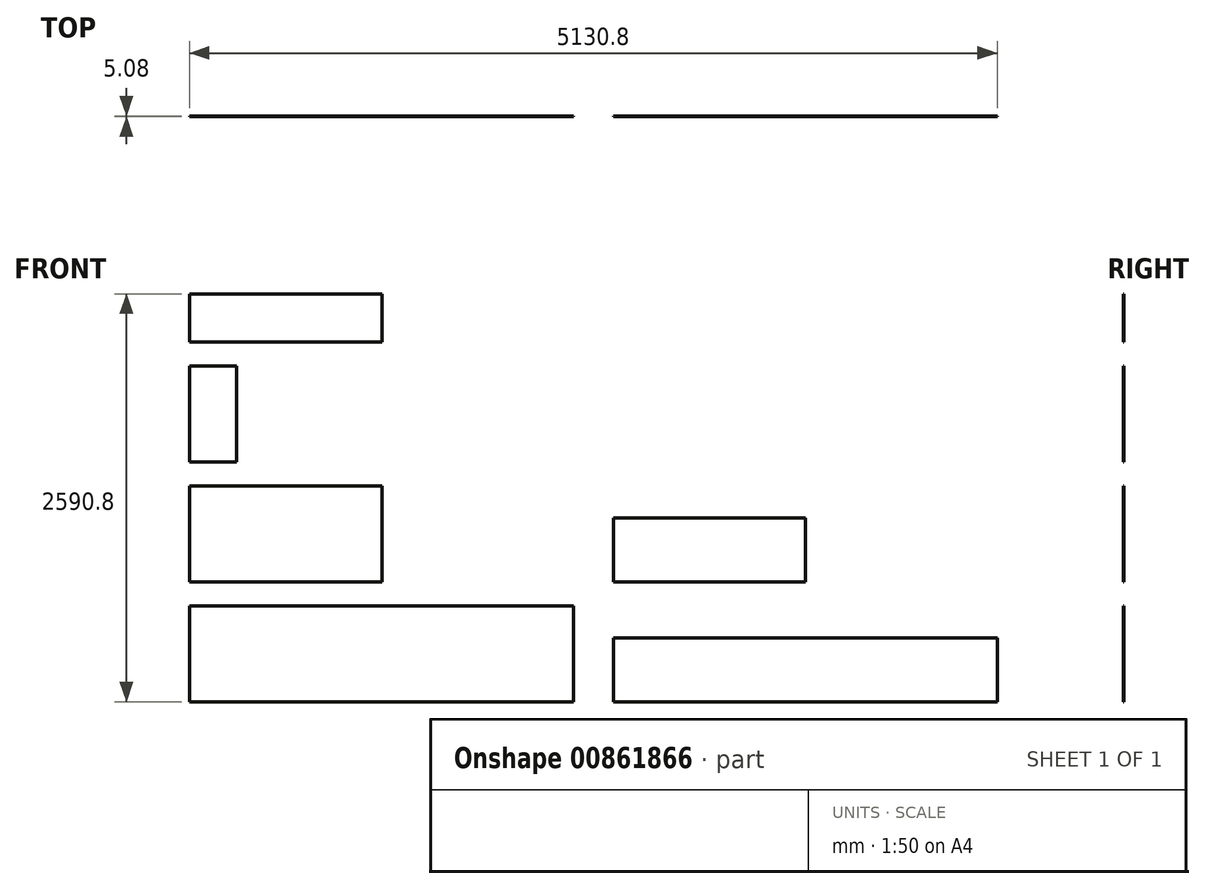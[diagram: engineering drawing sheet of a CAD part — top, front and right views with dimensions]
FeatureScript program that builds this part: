
annotation { "Feature Type Name" : "Feature", "Feature Type Description" : "" }
export const myFeature = defineFeature(function(context is Context, id is Id, definition is map)
    precondition{}
    {
        {
            var Q0;
            Q0=qCreatedBy(makeId("Front.planeOp"),FACE);
            var sketch = newSketch(context, id + "F0", { "sketchPlane" : qUnion([Q0])});
            skLineSegment(sketch, "E0.bottom", {"start": v(1219.2, -304.8) * mm, "end": v(-1219.2, -304.8) * mm});
            skLineSegment(sketch, "E0.top", {"start": v(1219.2, 304.8) * mm, "end": v(-1219.2, 304.8) * mm});
            skLineSegment(sketch, "E0.left", {"start": v(1219.2, -304.8) * mm, "end": v(1219.2, 304.8) * mm});
            skLineSegment(sketch, "E0.right", {"start": v(-1219.2, -304.8) * mm, "end": v(-1219.2, 304.8) * mm});
            skPoint(sketch, "E0.middle", {"position": v(0, 0) * mm});
            skSolve(sketch);
        }
        {
            var Q0;
            Q0=makeQuery(id+"F0.imprint","IMPRINT",FACE,{"disambiguationData":[TD([[makeQuery(id+"F0.imprint","IMPRINT",EDGE,{"derivedFrom":sQuery(id+"F0.wireOp",EDGE,"E0.bottom")}),-1.0]])]});
            extrude(context, id + "F1", {"entities" : qUnion([Q0]), "depth" : 5.08 * mm});
        }
        {
            var Q0;
            Q0=makeQuery(id+"F1.opExtrude","SWEPT_BODY",BODY,{"disambiguationData":[OSD([sQuery(id+"F0.wireOp",EDGE,"E0.bottom"),sQuery(id+"F0.wireOp",EDGE,"E0.top"),sQuery(id+"F0.wireOp",EDGE,"E0.left"),sQuery(id+"F0.wireOp",EDGE,"E0.right")])]});
            transform(context, id + "F2", {"entities" : qUnion([Q0]), "transformType" : TransformType.TRANSLATION_3D, "dx" : 0 * mm, "dy" : 0 * mm, "dz" : 914.4 * mm, "makeCopy" : true});
        }
        {
            var Q0;
            Q0=makeQuery(id+"F2.opPattern","COPY",FACE,{"derivedFrom":makeQuery(id+"F1.opExtrude","SWEPT_FACE",FACE,{"disambiguationData":[OSD([sQuery(id+"F0.wireOp",EDGE,"E0.left")])]}),"instanceName":"1"});
            extrude(context, id + "F3", {"entities" : qUnion([Q0]), "operationType" : NewBodyOperationType.ADD, "depth" : 609.6 * mm});
        }
        {
            var Q0;
            Q0=makeQuery(id+"F2.opPattern","COPY",BODY,{"derivedFrom":makeQuery(id+"F1.opExtrude","SWEPT_BODY",BODY,{"disambiguationData":[OSD([sQuery(id+"F0.wireOp",EDGE,"E0.bottom"),sQuery(id+"F0.wireOp",EDGE,"E0.top"),sQuery(id+"F0.wireOp",EDGE,"E0.left"),sQuery(id+"F0.wireOp",EDGE,"E0.right")])]}),"instanceName":"1"});
            deleteBodies(context, id + "F4", {"entities" : qUnion([Q0])});
        }
        {
            var Q0;
            Q0=makeQuery(id+"F1.opExtrude","SWEPT_BODY",BODY,{"disambiguationData":[OSD([sQuery(id+"F0.wireOp",EDGE,"E0.bottom"),sQuery(id+"F0.wireOp",EDGE,"E0.top"),sQuery(id+"F0.wireOp",EDGE,"E0.left"),sQuery(id+"F0.wireOp",EDGE,"E0.right")])]});
            transform(context, id + "F5", {"entities" : qUnion([Q0]), "transformType" : TransformType.TRANSLATION_3D, "dx" : 0 * mm, "dy" : 0 * mm, "dz" : 762 * mm, "makeCopy" : true});
        }
        {
            var Q0;
            Q0=makeQuery(id+"F5.opPattern","COPY",FACE,{"derivedFrom":makeQuery(id+"F1.opExtrude","SWEPT_FACE",FACE,{"disambiguationData":[OSD([sQuery(id+"F0.wireOp",EDGE,"E0.left")])]}),"instanceName":"1"});
            extrude(context, id + "F6", {"entities" : qUnion([Q0]), "operationType" : NewBodyOperationType.REMOVE, "oppositeDirection" : true, "depth" : 1219.2 * mm});
        }
        {
            var Q0;
            Q0=makeQuery(id+"F5.opPattern","COPY",BODY,{"derivedFrom":makeQuery(id+"F1.opExtrude","SWEPT_BODY",BODY,{"disambiguationData":[OSD([sQuery(id+"F0.wireOp",EDGE,"E0.bottom"),sQuery(id+"F0.wireOp",EDGE,"E0.top"),sQuery(id+"F0.wireOp",EDGE,"E0.left"),sQuery(id+"F0.wireOp",EDGE,"E0.right")])]}),"instanceName":"1"});
            transform(context, id + "F7", {"entities" : qUnion([Q0]), "transformType" : TransformType.TRANSLATION_3D, "dx" : 0 * mm, "dy" : 0 * mm, "dz" : 762 * mm, "makeCopy" : true});
        }
        {
            var Q0;
            Q0=makeQuery(id+"F7.opPattern","COPY",FACE,{"derivedFrom":makeQuery(id+"F6.boolean.opBoolean","COPY",FACE,{"derivedFrom":makeQuery(id+"F6.opExtrude","CAP_FACE",FACE,{"disambiguationData":[OSD([sQuery(id+"F0.wireOp",EDGE,"E0.left")])],"isStart":false})}),"instanceName":"1"});
            extrude(context, id + "F8", {"entities" : qUnion([Q0]), "operationType" : NewBodyOperationType.REMOVE, "oppositeDirection" : true, "depth" : 304.8 * mm});
        }
        {
            var Q0;
            Q0=makeQuery(id+"F8.boolean.opBoolean","COPY",FACE,{"derivedFrom":makeQuery(id+"F8.opExtrude","CAP_FACE",FACE,{"disambiguationData":[OSD([sQuery(id+"F0.wireOp",EDGE,"E0.left")])],"isStart":false})});
            extrude(context, id + "F9", {"entities" : qUnion([Q0]), "operationType" : NewBodyOperationType.REMOVE, "oppositeDirection" : true, "depth" : 609.6 * mm});
        }
        {
            var Q0;
            Q0=makeQuery(id+"F9.boolean.opBoolean","COPY",FACE,{"derivedFrom":makeQuery(id+"F9.opExtrude","CAP_FACE",FACE,{"disambiguationData":[OSD([sQuery(id+"F0.wireOp",EDGE,"E0.left")])],"isStart":false})});
            extrude(context, id + "F10", {"entities" : qUnion([Q0]), "operationType" : NewBodyOperationType.ADD, "depth" : 6.35 * mm});
        }
        {
            var Q0;
            Q0=makeQuery(id+"F10.opExtrude","CAP_FACE",FACE,{"disambiguationData":[OSD([sQuery(id+"F0.wireOp",EDGE,"E0.left")])],"isStart":false});
            extrude(context, id + "F11", {"entities" : qUnion([Q0]), "operationType" : NewBodyOperationType.REMOVE, "oppositeDirection" : true, "depth" : 11.43 * mm});
        }
        {
            var Q0;
            Q0=makeQuery(id+"F6.boolean.opBoolean","COPY",FACE,{"derivedFrom":makeQuery(id+"F6.opExtrude","CAP_FACE",FACE,{"disambiguationData":[OSD([sQuery(id+"F0.wireOp",EDGE,"E0.left")])],"isStart":false})});
            extrude(context, id + "F12", {"entities" : qUnion([Q0]), "operationType" : NewBodyOperationType.ADD, "depth" : 5.08 * mm});
        }
        {
            var Q0;
            Q0=makeQuery(id+"F5.opPattern","COPY",BODY,{"derivedFrom":makeQuery(id+"F1.opExtrude","SWEPT_BODY",BODY,{"disambiguationData":[OSD([sQuery(id+"F0.wireOp",EDGE,"E0.bottom"),sQuery(id+"F0.wireOp",EDGE,"E0.top"),sQuery(id+"F0.wireOp",EDGE,"E0.left"),sQuery(id+"F0.wireOp",EDGE,"E0.right")])]}),"instanceName":"1"});
            transform(context, id + "F13", {"entities" : qUnion([Q0]), "transformType" : TransformType.TRANSLATION_3D, "dx" : 0 * mm, "dy" : 0 * mm, "dz" : 1524 * mm, "makeCopy" : true});
        }
        {
            var Q0;
            {var subQ0=sQuery(id+"F0.wireOp",EDGE,"E0.top");Q0=makeQuery(id+"F13.opPattern","COPY",FACE,{"derivedFrom":makeQuery(id+"F12.boolean.opBoolean","MERGE",FACE,{"derivedFrom":[makeQuery(id+"F5.opPattern","COPY",FACE,{"derivedFrom":makeQuery(id+"F1.opExtrude","SWEPT_FACE",FACE,{"disambiguationData":[OSD([subQ0])]}),"instanceName":"1"}),makeQuery(id+"F12.opExtrude","SWEPT_FACE",FACE,{"disambiguationData":[OSD([subQ0,sQuery(id+"F0.wireOp",EDGE,"E0.left")])]})]}),"instanceName":"1"});}
            extrude(context, id + "F14", {"entities" : qUnion([Q0]), "operationType" : NewBodyOperationType.REMOVE, "oppositeDirection" : true, "depth" : 304.8 * mm});
        }
        {
            var Q0;
            Q0=makeQuery(id+"F5.opPattern","COPY",BODY,{"derivedFrom":makeQuery(id+"F1.opExtrude","SWEPT_BODY",BODY,{"disambiguationData":[OSD([sQuery(id+"F0.wireOp",EDGE,"E0.bottom"),sQuery(id+"F0.wireOp",EDGE,"E0.top"),sQuery(id+"F0.wireOp",EDGE,"E0.left"),sQuery(id+"F0.wireOp",EDGE,"E0.right")])]}),"instanceName":"1"});
            transform(context, id + "F15", {"entities" : qUnion([Q0]), "transformType" : TransformType.TRANSLATION_3D, "dx" : 2692.4 * mm, "dy" : 0 * mm, "dz" : 0 * mm, "makeCopy" : true});
        }
        {
            var Q0;
            {var subQ0=sQuery(id+"F0.wireOp",EDGE,"E0.top");Q0=makeQuery(id+"F15.opPattern","COPY",FACE,{"derivedFrom":makeQuery(id+"F12.boolean.opBoolean","MERGE",FACE,{"derivedFrom":[makeQuery(id+"F5.opPattern","COPY",FACE,{"derivedFrom":makeQuery(id+"F1.opExtrude","SWEPT_FACE",FACE,{"disambiguationData":[OSD([subQ0])]}),"instanceName":"1"}),makeQuery(id+"F12.opExtrude","SWEPT_FACE",FACE,{"disambiguationData":[OSD([subQ0,sQuery(id+"F0.wireOp",EDGE,"E0.left")])]})]}),"instanceName":"1"});}
            extrude(context, id + "F16", {"entities" : qUnion([Q0]), "operationType" : NewBodyOperationType.REMOVE, "oppositeDirection" : true, "depth" : 203.2 * mm});
        }
        {
            var Q0;
            Q0=makeQuery(id+"F1.opExtrude","SWEPT_BODY",BODY,{"disambiguationData":[OSD([sQuery(id+"F0.wireOp",EDGE,"E0.bottom"),sQuery(id+"F0.wireOp",EDGE,"E0.top"),sQuery(id+"F0.wireOp",EDGE,"E0.left"),sQuery(id+"F0.wireOp",EDGE,"E0.right")])]});
            transform(context, id + "F17", {"entities" : qUnion([Q0]), "transformType" : TransformType.TRANSLATION_3D, "dx" : 2692.4 * mm, "dy" : 0 * mm, "dz" : 0 * mm, "makeCopy" : true});
        }
        {
            var Q0;
            Q0=makeQuery(id+"F17.opPattern","COPY",FACE,{"derivedFrom":makeQuery(id+"F1.opExtrude","SWEPT_FACE",FACE,{"disambiguationData":[OSD([sQuery(id+"F0.wireOp",EDGE,"E0.top")])]}),"instanceName":"1"});
            extrude(context, id + "F18", {"entities" : qUnion([Q0]), "operationType" : NewBodyOperationType.REMOVE, "oppositeDirection" : true, "depth" : 203.2 * mm});
        }
        {
            var Q0;
            Q0=makeQuery(id+"F15.opPattern","COPY",FACE,{"derivedFrom":makeQuery(id+"F12.opExtrude","CAP_FACE",FACE,{"disambiguationData":[OSD([sQuery(id+"F0.wireOp",EDGE,"E0.left")])],"isStart":false}),"instanceName":"1"});
            extrude(context, id + "F19", {"entities" : qUnion([Q0]), "operationType" : NewBodyOperationType.REMOVE, "oppositeDirection" : true, "depth" : 5.08 * mm});
        }
    });
